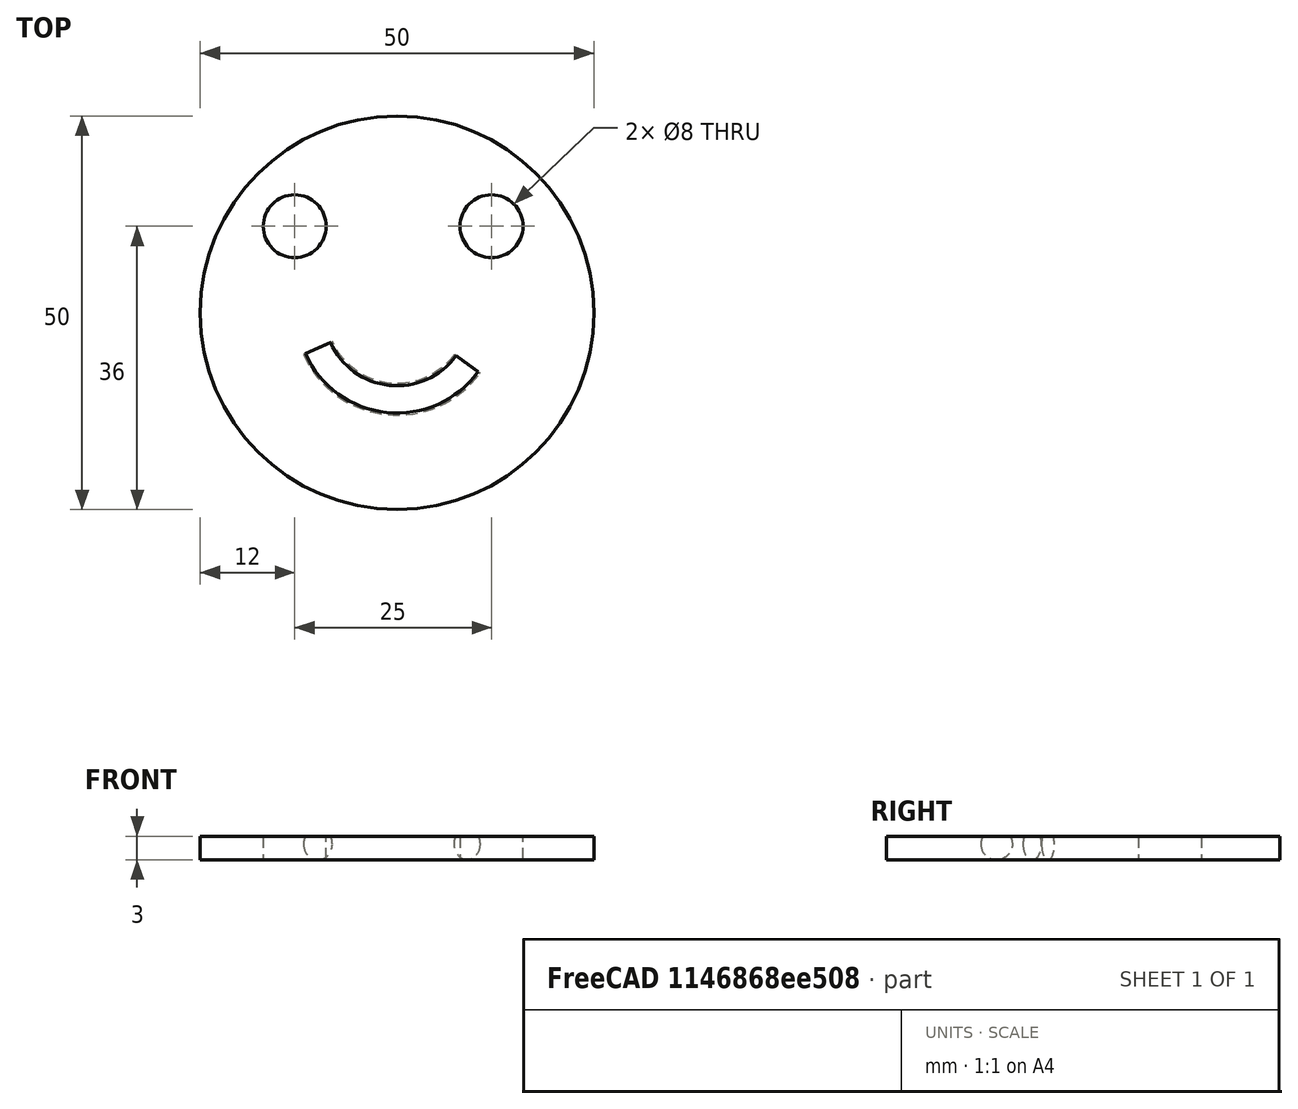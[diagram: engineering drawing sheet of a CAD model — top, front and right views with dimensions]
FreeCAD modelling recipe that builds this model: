
FCSTD DOCUMENT  (FreeCAD 0.18.4R)
Label: Ejercicio1Video15
License: All rights reserved
LicenseURL: http://en.wikipedia.org/wiki/All_rights_reserved
objects: Part::Cylinder×3, Part::Cut×2, Part::Fuse×1, Part::Torus×1
note: 7 computed .brp shape members not serialized (recipe doc carries the construction recipe); baked Part::Feature solids carry a one-line shape summary decoded from their .brp

FEATURE [Part::Cylinder] Cylinder  label="Cilindro"
  Angle = 360
  AttacherType = Attacher::AttachEngine3D
  Height = 3
  Radius = 25
FEATURE [Part::Cylinder] Cylinder001  label="Cilindro001"
  Angle = 360
  AttacherType = Attacher::AttachEngine3D
  Height = 10
  Placement = pos=(-13,11,-2) rot=(0,0,1;0rad)
  Radius = 4
FEATURE [Part::Cylinder] Cylinder002  label="Cilindro002"
  Angle = 360
  AttacherType = Attacher::AttachEngine3D
  Height = 10
  Placement = pos=(12,11,-2) rot=(0,0,1;0rad)
  Radius = 4
FEATURE [Part::Fuse] Fusion
  Base = -> Cylinder001
  Tool = -> Cylinder002
FEATURE [Part::Cut] Cut
  Base = -> Cylinder
  Tool = -> Fusion
FEATURE [Part::Torus] Torus  label="Toro"
  Angle1 = -180
  Angle2 = 180
  Angle3 = 120
  AttacherType = Attacher::AttachEngine3D
  Placement = pos=(0,0,2) rot=(0,0,1;3.56047rad)
  Radius1 = 11
  Radius2 = 2
FEATURE [Part::Cut] Cut001
  Base = -> Cut
  Refine = true
  Tool = -> Torus
